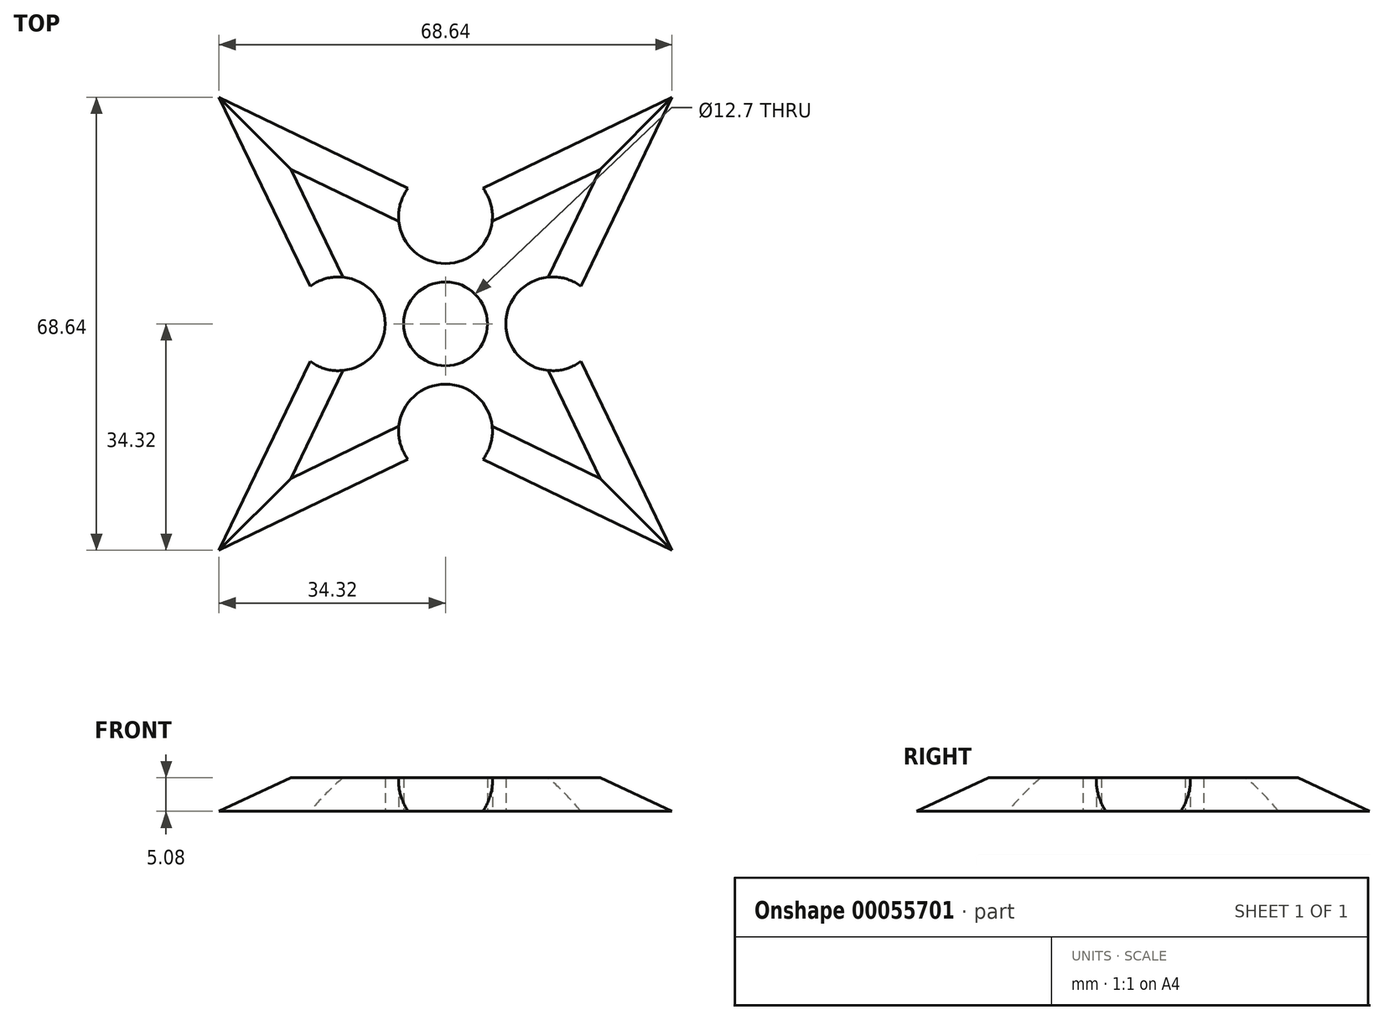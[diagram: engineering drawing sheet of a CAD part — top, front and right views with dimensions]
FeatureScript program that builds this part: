
annotation { "Feature Type Name" : "Feature", "Feature Type Description" : "" }
export const myFeature = defineFeature(function(context is Context, id is Id, definition is map)
    precondition{}
    {
        {
            var Q0;
            Q0=qCreatedBy(makeId("Top.planeOp"),FACE);
            var sketch = newSketch(context, id + "F0", { "sketchPlane" : qUnion([Q0])});
            skCircle(sketch, "E0", {"center": v(0, 0) * mm, "radius": 6.35 * mm});
            skCircle(sketch, "E1", {"center": v(0, 0) * mm, "radius": 17.78 * mm});
            skLineSegment(sketch, "E2", {"start": v(0, 17.78) * mm, "end": v(-34.32, 34.32) * mm});
            skLineSegment(sketch, "E3", {"start": v(-34.32, 34.32) * mm, "end": v(-17.78, 0) * mm});
            skLineSegment(sketch, "E4", {"start": v(-17.78, 0) * mm, "end": v(-34.32, -34.32) * mm});
            skLineSegment(sketch, "E5", {"start": v(-34.32, -34.32) * mm, "end": v(0, -17.78) * mm});
            skLineSegment(sketch, "E6", {"start": v(0, -17.78) * mm, "end": v(34.32, -34.32) * mm});
            skLineSegment(sketch, "E7", {"start": v(34.32, -34.32) * mm, "end": v(17.78, 0) * mm});
            skLineSegment(sketch, "E8", {"start": v(17.78, 0) * mm, "end": v(34.32, 34.32) * mm});
            skLineSegment(sketch, "E9", {"start": v(34.32, 34.32) * mm, "end": v(0, 17.78) * mm});
            skPoint(sketch, "E10", {"position": v(-16.26, 0) * mm});
            skPoint(sketch, "E11", {"position": v(0, 16.26) * mm});
            skPoint(sketch, "E12", {"position": v(16.26, 0) * mm});
            skPoint(sketch, "E13", {"position": v(0, -16.26) * mm});
            skCircle(sketch, "E14", {"center": v(-16.26, 0) * mm, "radius": 7.11 * mm});
            skCircle(sketch, "E15", {"center": v(0, -16.26) * mm, "radius": 7.11 * mm});
            skCircle(sketch, "E16", {"center": v(16.26, 0) * mm, "radius": 7.11 * mm});
            skCircle(sketch, "E17", {"center": v(0, 16.26) * mm, "radius": 7.11 * mm});
            skSolve(sketch);
        }
        {
            var Q0;
            {var subQ3=sQuery(id+"F0.wireOp",EDGE,"E1");var subQ7=sQuery(id+"F0.wireOp",EDGE,"E17");var subQ9=makeQuery(id+"F0.imprint","INTERSECT",VERTEX,{"disambiguationData":[OD(1.0)],"derivedFrom":[subQ3,subQ7]});Q0=makeQuery(id+"F0.imprint","IMPRINT",FACE,{"disambiguationData":[TD([[makeQuery(id+"F0.imprint","IMPRINT",EDGE,{"disambiguationData":[TD([[subQ9,-1.0]])],"derivedFrom":subQ3}),-1.0]])]});}
            var Q1;
            Q1=makeQuery(id+"F0.imprint","IMPRINT",FACE,{"disambiguationData":[TD([[makeQuery(id+"F0.imprint","IMPRINT",EDGE,{"derivedFrom":sQuery(id+"F0.wireOp",EDGE,"E0")}),-1.0]])]});
            var Q2;
            {var subQ0=sQuery(id+"F0.wireOp",EDGE,"E16");var subQ3=sQuery(id+"F0.wireOp",EDGE,"E1");var subQ4=makeQuery(id+"F0.imprint","INTERSECT",VERTEX,{"disambiguationData":[OD(0.0)],"derivedFrom":[subQ3,subQ0]});Q2=makeQuery(id+"F0.imprint","IMPRINT",FACE,{"disambiguationData":[TD([[makeQuery(id+"F0.imprint","IMPRINT",EDGE,{"disambiguationData":[TD([[subQ4,-1.0]])],"derivedFrom":subQ3}),-1.0]])]});}
            var Q3;
            {var subQ5=sQuery(id+"F0.wireOp",EDGE,"E15");var subQ7=sQuery(id+"F0.wireOp",EDGE,"E1");var subQ8=makeQuery(id+"F0.imprint","INTERSECT",VERTEX,{"disambiguationData":[OD(1.0)],"derivedFrom":[subQ7,subQ5]});Q3=makeQuery(id+"F0.imprint","IMPRINT",FACE,{"disambiguationData":[TD([[makeQuery(id+"F0.imprint","IMPRINT",EDGE,{"disambiguationData":[TD([[subQ8,-1.0]])],"derivedFrom":subQ7}),-1.0]])]});}
            var Q4;
            {var subQ0=sQuery(id+"F0.wireOp",EDGE,"E14");var subQ3=sQuery(id+"F0.wireOp",EDGE,"E1");var subQ4=makeQuery(id+"F0.imprint","INTERSECT",VERTEX,{"disambiguationData":[OD(1.0)],"derivedFrom":[subQ3,subQ0]});Q4=makeQuery(id+"F0.imprint","IMPRINT",FACE,{"disambiguationData":[TD([[makeQuery(id+"F0.imprint","IMPRINT",EDGE,{"disambiguationData":[TD([[subQ4,-1.0]])],"derivedFrom":subQ3}),-1.0]])]});}
            extrude(context, id + "F1", {"entities" : qUnion([Q0, Q1, Q2, Q3, Q4]), "depth" : 5.08 * mm});
        }
        {
            var Q0;
            Q0=makeQuery(id+"F1.opExtrude","CAP_EDGE",EDGE,{"disambiguationData":[OSD([sQuery(id+"F0.wireOp",EDGE,"E3")])],"isStart":false});
            var Q1;
            Q1=makeQuery(id+"F1.opExtrude","CAP_EDGE",EDGE,{"disambiguationData":[OSD([sQuery(id+"F0.wireOp",EDGE,"E2")])],"isStart":false});
            var Q2;
            Q2=makeQuery(id+"F1.opExtrude","CAP_EDGE",EDGE,{"disambiguationData":[OSD([sQuery(id+"F0.wireOp",EDGE,"E9")])],"isStart":false});
            var Q3;
            Q3=makeQuery(id+"F1.opExtrude","CAP_EDGE",EDGE,{"disambiguationData":[OSD([sQuery(id+"F0.wireOp",EDGE,"E8")])],"isStart":false});
            var Q4;
            Q4=makeQuery(id+"F1.opExtrude","CAP_EDGE",EDGE,{"disambiguationData":[OSD([sQuery(id+"F0.wireOp",EDGE,"E7")])],"isStart":false});
            var Q5;
            Q5=makeQuery(id+"F1.opExtrude","CAP_EDGE",EDGE,{"disambiguationData":[OSD([sQuery(id+"F0.wireOp",EDGE,"E6")])],"isStart":false});
            var Q6;
            Q6=makeQuery(id+"F1.opExtrude","CAP_EDGE",EDGE,{"disambiguationData":[OSD([sQuery(id+"F0.wireOp",EDGE,"E5")])],"isStart":false});
            var Q7;
            Q7=makeQuery(id+"F1.opExtrude","CAP_EDGE",EDGE,{"disambiguationData":[OSD([sQuery(id+"F0.wireOp",EDGE,"E4")])],"isStart":false});
            chamfer(context, id + "F2", {"entities" : qUnion([Q0, Q1, Q2, Q3, Q4, Q5, Q6, Q7]), "width" : 5.08 * mm, "tangentPropagation" : true});
        }
    });
